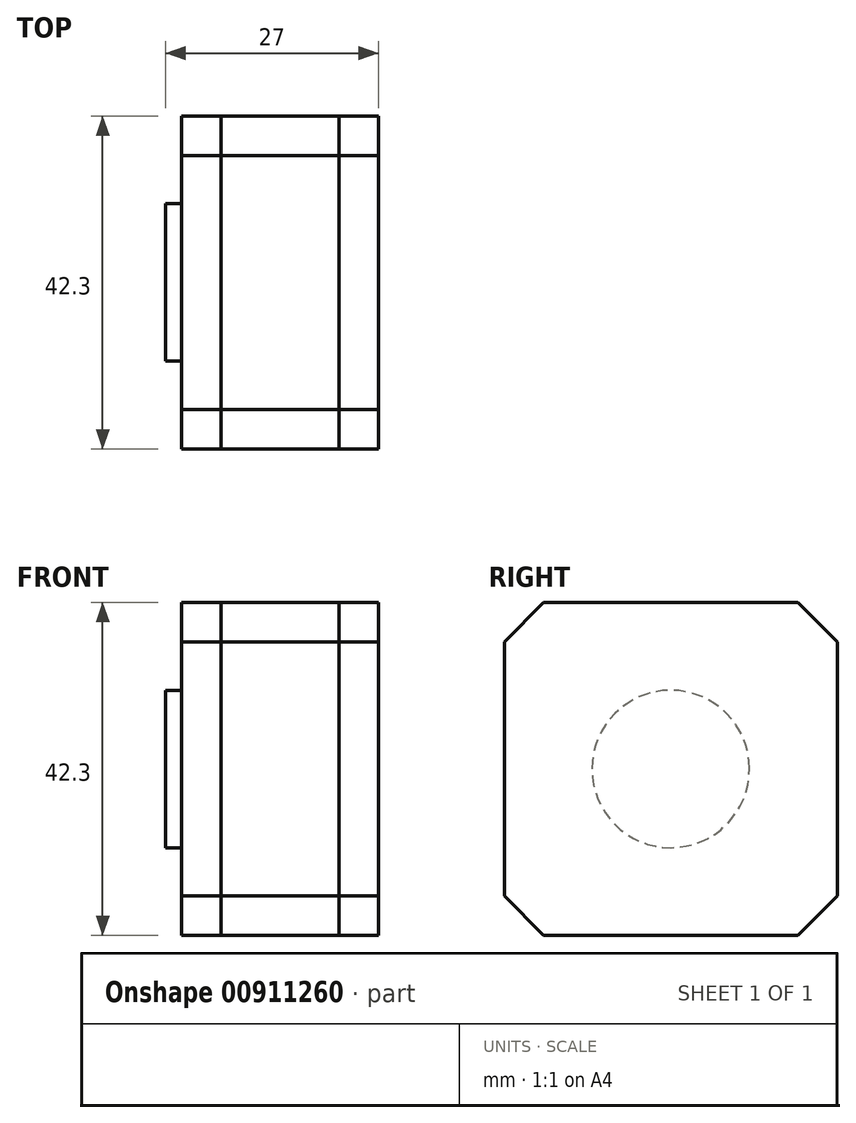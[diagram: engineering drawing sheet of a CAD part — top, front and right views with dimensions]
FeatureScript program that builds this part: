
annotation { "Feature Type Name" : "Feature", "Feature Type Description" : "" }
export const myFeature = defineFeature(function(context is Context, id is Id, definition is map)
    precondition{}
    {
        {
            var Q0;
            Q0=qCreatedBy(makeId("Right.planeOp"),FACE);
            var sketch = newSketch(context, id + "F0", { "sketchPlane" : qUnion([Q0])});
            skLineSegment(sketch, "E0.bottom", {"start": v(21.15, 21.15) * mm, "end": v(-21.15, 21.15) * mm});
            skLineSegment(sketch, "E0.top", {"start": v(21.15, -21.15) * mm, "end": v(-21.15, -21.15) * mm});
            skLineSegment(sketch, "E0.left", {"start": v(21.15, 21.15) * mm, "end": v(21.15, -21.15) * mm});
            skLineSegment(sketch, "E0.right", {"start": v(-21.15, 21.15) * mm, "end": v(-21.15, -21.15) * mm});
            skPoint(sketch, "E0.middle", {"position": v(0, 0) * mm});
            skSolve(sketch);
        }
        {
            var Q0;
            Q0=makeQuery(id+"F0.imprint","IMPRINT",FACE,{"disambiguationData":[TD([[makeQuery(id+"F0.imprint","IMPRINT",EDGE,{"derivedFrom":sQuery(id+"F0.wireOp",EDGE,"E0.bottom")}),1.0]])]});
            extrude(context, id + "F1", {"entities" : qUnion([Q0]), "depth" : 5 * mm, "offsetDistance" : 25 * mm});
        }
        {
            var Q0;
            Q0=makeQuery(id+"F1.opExtrude","SWEPT_EDGE",EDGE,{"disambiguationData":[OSD([sQuery(id+"F0.wireOp",EDGE,"E0.bottom"),sQuery(id+"F0.wireOp",EDGE,"E0.right")])]});
            var Q1;
            Q1=makeQuery(id+"F1.opExtrude","SWEPT_EDGE",EDGE,{"disambiguationData":[OSD([sQuery(id+"F0.wireOp",EDGE,"E0.top"),sQuery(id+"F0.wireOp",EDGE,"E0.right")])]});
            var Q2;
            Q2=makeQuery(id+"F1.opExtrude","SWEPT_EDGE",EDGE,{"disambiguationData":[OSD([sQuery(id+"F0.wireOp",EDGE,"E0.top"),sQuery(id+"F0.wireOp",EDGE,"E0.left")])]});
            var Q3;
            Q3=makeQuery(id+"F1.opExtrude","SWEPT_EDGE",EDGE,{"disambiguationData":[OSD([sQuery(id+"F0.wireOp",EDGE,"E0.bottom"),sQuery(id+"F0.wireOp",EDGE,"E0.left")])]});
            chamfer(context, id + "F2", {"entities" : qUnion([Q0, Q1, Q2, Q3]), "width" : 5 * mm, "tangentPropagation" : true});
        }
        {
            var Q0;
            Q0=makeQuery(id+"F1.opExtrude","CAP_FACE",FACE,{"disambiguationData":[OSD([sQuery(id+"F0.wireOp",EDGE,"E0.bottom"),sQuery(id+"F0.wireOp",EDGE,"E0.top"),sQuery(id+"F0.wireOp",EDGE,"E0.left"),sQuery(id+"F0.wireOp",EDGE,"E0.right")])],"isStart":false});
            extrude(context, id + "F3", {"entities" : qUnion([Q0]), "depth" : 15 * mm, "offsetDistance" : 25 * mm});
        }
        {
            var Q0;
            Q0=makeQuery(id+"F3.opExtrude","CAP_FACE",FACE,{"disambiguationData":[OSD([sQuery(id+"F0.wireOp",EDGE,"E0.bottom"),sQuery(id+"F0.wireOp",EDGE,"E0.top"),sQuery(id+"F0.wireOp",EDGE,"E0.left"),sQuery(id+"F0.wireOp",EDGE,"E0.right")])],"isStart":false});
            extrude(context, id + "F4", {"entities" : qUnion([Q0]), "depth" : 5 * mm, "offsetDistance" : 25 * mm});
        }
        {
            var Q0;
            Q0=makeQuery(id+"F1.opExtrude","CAP_FACE",FACE,{"disambiguationData":[OSD([sQuery(id+"F0.wireOp",EDGE,"E0.bottom"),sQuery(id+"F0.wireOp",EDGE,"E0.top"),sQuery(id+"F0.wireOp",EDGE,"E0.left"),sQuery(id+"F0.wireOp",EDGE,"E0.right")])],"isStart":true});
            var sketch = newSketch(context, id + "F5", { "sketchPlane" : qUnion([Q0])});
            skCircle(sketch, "E1", {"center": v(0, 0) * mm, "radius": 10 * mm});
            skSolve(sketch);
        }
        {
            var Q0;
            Q0=makeQuery(id+"F5.imprint","IMPRINT",FACE,{"disambiguationData":[TD([[makeQuery(id+"F5.imprint","IMPRINT",EDGE,{"derivedFrom":sQuery(id+"F5.wireOp",EDGE,"E1")}),1.0]])]});
            extrude(context, id + "F6", {"entities" : qUnion([Q0]), "operationType" : NewBodyOperationType.ADD, "depth" : 2 * mm, "offsetDistance" : 25 * mm});
        }
    });
